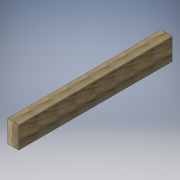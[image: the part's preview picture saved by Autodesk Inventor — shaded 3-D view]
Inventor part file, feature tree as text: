
AUTODESK INVENTOR PART (.ipt)
format: ipt  version: 2016 (Build 200138000, 138)  size: 106,496 bytes
history: native  units: in
note: dims shown in document units (in); Inventor stores cm internally (conversion verified against a paired STEP export)
features: extrude x1, sketch x1
ambient origin geometry x8: Origin, YZ Plane, XZ Plane, XY Plane, X Axis, Y Axis, Z Axis, Center Point
bodies: Solid1 (feature_tree)
feature tree (2):
  extrude  "Extrusion1"  Depth=4.0in
  sketch  "Sketch1"  dims[d0=2.0in d1=4.0in d2=28.0in d3=0.0in]
